# Revit family: RN 57040 Optifitt-Press-Übergang
name_source: partatom
category: Rohrformteile
units: mm (PartAtom-declared; Revit-internal decimal feet)

## family parameters
Arbeitsebenenbasiert = Nein
Beim Laden mit Abzugskörper schneiden = Nein
Bemaßung runder Anschluss = Durchmesser verwenden
Gemeinsam genutzt = Nein
Immer vertikal = Ja
Teiletyp = Verbindung

## types (7) — shared parameters
1.010.00.2 Blattnummer der Richtlinie = 29
1.010.00.3 Ausgabedatum (Monat) der Richtlinie = 201308
1.010.00.4 Herstellername = R. Nussbaum AG
1.010.00.5 Revisionsdatum der Datei = 20190521
1.010.00.6 Webadresse des Herstellers = http://www.nussbaum.ch
1.100.00.4 Produktbezeichnung = Versorgung
1.110.00.2 Index = 2
1.110.00.4 Produktbezeichnung = Optifitt-Press
1.960/3L.00.8 Link (URL) = https://www.nussbaum.ch
29.700.00.4 Produktname = Optifitt-Press-Übergang, auf Optipress-Aquaplus
29.700.00.5 Produktkennung = 2
29.700.00.6 Querschnittsform = 1
29.700.00.7 Nennweitensystem = DN
29.700.00.8 Nenndrucksystem = PN
29.710.02.4 Nenndruck = 16
29.710.02.5 max. zul. Überdruck [hPa] = 1600
29.710.02.7 max. zul. Dauer-Betriebsdruck [hPa] = 1600
29.710.02.9 max. zul. Dauer-Betriebstemperatur [°C] = 95
Beschreibung = Optifitt-Press-Übergang
Connector Visibility = Nein
EnclosingSpace Visibility = Nein
Hersteller = R. Nussbaum AG
URL = https://www.nussbaum.ch

## per-type parameters (varying)
| type | 1.800.00.3 TGA-Nummer | 1.800.00.4 Kommentarfeld | 1.810.00.3 Hersteller-Bestellnummer | 1.810.00.4 DATANORM-Nummer | 1.810.00.6 GTIN-Nummer | 29.710.02.10 Formstück-Gewicht [kg] | 29.710.02.3 Benennung | CONNECTOR0_DIAMETER_dX_0r | CONNECTOR0_dX_01 | CONNECTOR0_ref_dX | CONNECTOR1_DIAMETER_dX_0r | CONNECTOR1_dX_00 | CONNECTOR1_dX_01 | CONNECTOR1_ref_dX | Modell | R. Nussbaum AG 57040.22 de Visibility | R. Nussbaum AG 57040.23 de Visibility | R. Nussbaum AG 57040.24 de Visibility | R. Nussbaum AG 57040.25 de Visibility | R. Nussbaum AG 57040.26 de Visibility | R. Nussbaum AG 57040.27 de Visibility | R. Nussbaum AG 57040.28 de Visibility | Typenkommentare |
| DN=50 | 01900200000000000000000000000000000000000000000018000000000000000007 | 57040.28, Optifitt-Press-Übergang, auf Optipress-Aquaplus, DN=50, L=98 | 57040.28 | 57040.28 | 7612945746443 | 0.45 | Optifitt-Press-Übergang, auf Optipress-Aquaplus, DN=50, L=98 | 50 mm | 50 mm | 50 mm | 50 mm | 58 mm | 98 mm | 58 mm | 57040.28 | Nein | Nein | Nein | Nein | Nein | Nein | Ja | Optifitt-Press-Übergang  DN=50 |
| DN=40 | 01900200000000000000000000000000000000000000000018000000000000000006 | 57040.27, Optifitt-Press-Übergang, auf Optipress-Aquaplus, DN=40, L=90 | 57040.27 | 57040.27 | 7612945746436 | 0.319 | Optifitt-Press-Übergang, auf Optipress-Aquaplus, DN=40, L=90 | 40 mm | 48 mm | 48 mm | 40 mm | 54 mm | 90 mm | 54 mm | 57040.27 | Nein | Nein | Nein | Nein | Nein | Ja | Nein | Optifitt-Press-Übergang  DN=40 |
| DN=32 | 01900200000000000000000000000000000000000000000018000000000000000005 | 57040.26, Optifitt-Press-Übergang, auf Optipress-Aquaplus, DN=32, L=78 | 57040.26 | 57040.26 | 7612945746429 | 0.239 | Optifitt-Press-Übergang, auf Optipress-Aquaplus, DN=32, L=78 | 32 mm | 46 mm | 46 mm | 32 mm | 52 mm | 78 mm | 52 mm | 57040.26 | Nein | Nein | Nein | Nein | Ja | Nein | Nein | Optifitt-Press-Übergang  DN=32 |
| DN=25 | 01900200000000000000000000000000000000000000000018000000000000000004 | 57040.25, Optifitt-Press-Übergang, auf Optipress-Aquaplus, DN=25, L=67 | 57040.25 | 57040.25 | 7612945746412 | 0.16 | Optifitt-Press-Übergang, auf Optipress-Aquaplus, DN=25, L=67 | 25 mm  [stored 0.082021 ft] | 34 mm | 34 mm | 25 mm  [stored 0.082021 ft] | 43 mm  [stored 0.141076 ft] | 67 mm | 43 mm  [stored 0.141076 ft] | 57040.25 | Nein | Nein | Nein | Ja | Nein | Nein | Nein | Optifitt-Press-Übergang  DN=25 |
| DN=20 | 01900200000000000000000000000000000000000000000018000000000000000003 | 57040.24, Optifitt-Press-Übergang, auf Optipress-Aquaplus, DN=20, L=58 | 57040.24 | 57040.24 | 7612945746405 | 0.105 | Optifitt-Press-Übergang, auf Optipress-Aquaplus, DN=20, L=58 | 20 mm | 29 mm | 29 mm | 20 mm | 34 mm | 58 mm | 34 mm | 57040.24 | Nein | Nein | Ja | Nein | Nein | Nein | Nein | Optifitt-Press-Übergang  DN=20 |
| DN=15 | 01900200000000000000000000000000000000000000000018000000000000000002 | 57040.23, Optifitt-Press-Übergang, auf Optipress-Aquaplus, DN=15, L=54 | 57040.23 | 57040.23 | 7612945746399 | 0.072 | Optifitt-Press-Übergang, auf Optipress-Aquaplus, DN=15, L=54 | 15 mm | 27 mm | 27 mm | 15 mm | 32 mm | 54 mm | 32 mm | 57040.23 | Nein | Ja | Nein | Nein | Nein | Nein | Nein | Optifitt-Press-Übergang  DN=15 |
| DN=15x12 | 01900200000000000000000000000000000000000000000018000000000000000001 | 57040.22, Optifitt-Press-Übergang, auf Optipress-Aquaplus, DN=15x12, L=55 | 57040.22 | 57040.22 | 7612945746382 | 0.069 | Optifitt-Press-Übergang, auf Optipress-Aquaplus, DN=15x12, L=55 | 15 mm | 27 mm | 27 mm | 12 mm  [stored 0.0393701 ft] | 33 mm | 55 mm  [stored 0.180446 ft] | 33 mm | 57040.22 | Ja | Nein | Nein | Nein | Nein | Nein | Nein | Optifitt-Press-Übergang  DN=15x12 |

note: [stored X ft] marks values corroborated as IEEE doubles in the binary element streams (Revit-internal decimal feet)

## geometry (parser evidence)
native form markers: Sweep x1
no freeform markers — native parametric forms only
